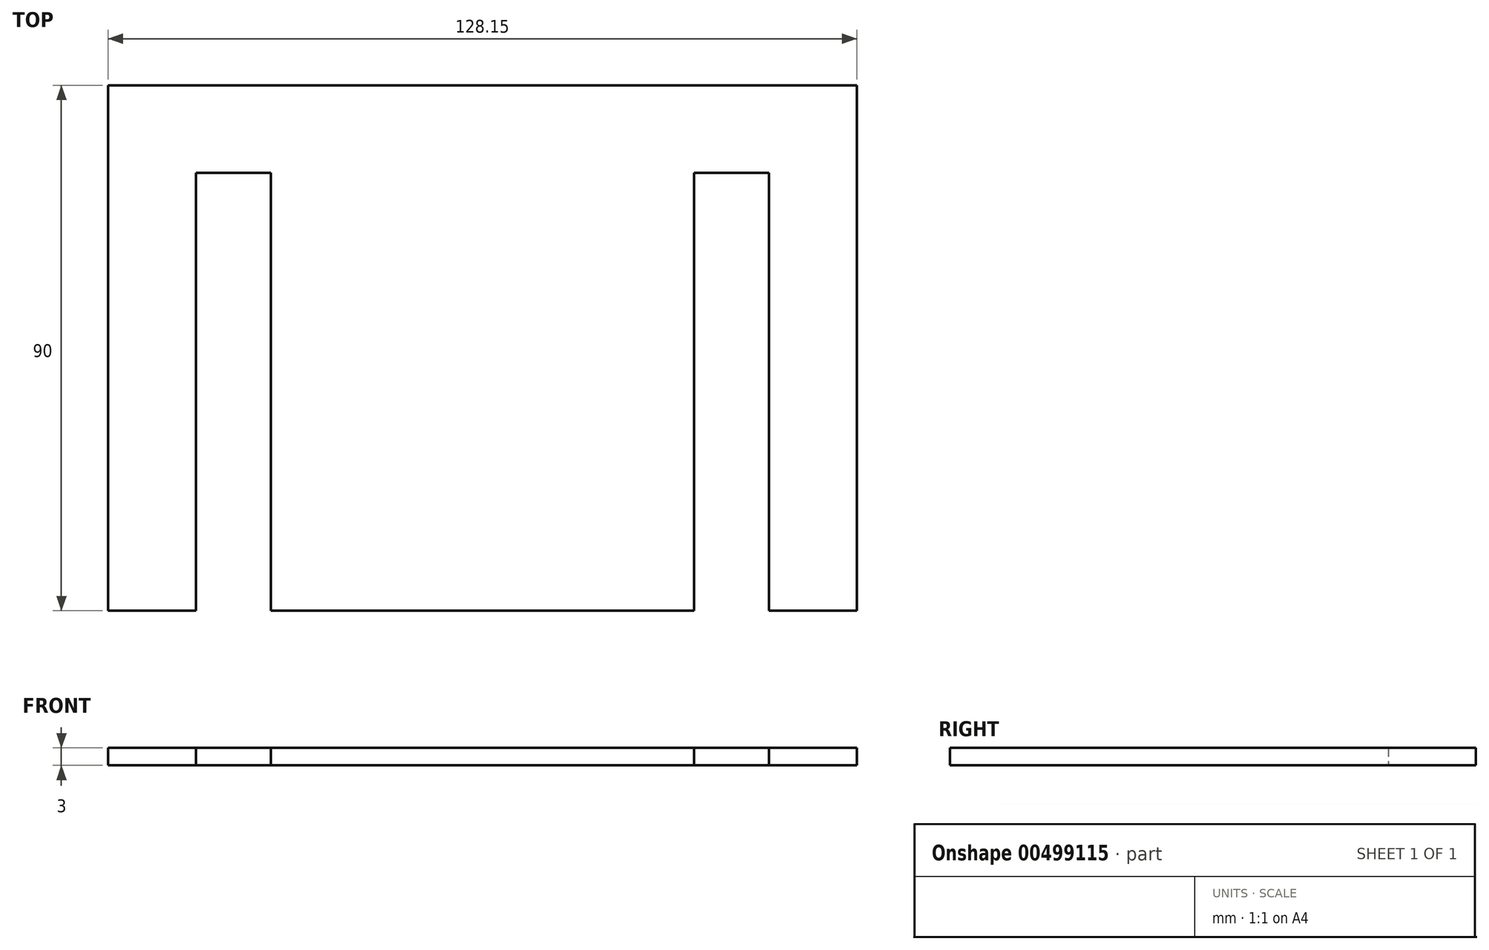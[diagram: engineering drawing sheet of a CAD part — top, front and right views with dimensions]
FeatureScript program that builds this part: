
annotation { "Feature Type Name" : "Feature", "Feature Type Description" : "" }
export const myFeature = defineFeature(function(context is Context, id is Id, definition is map)
    precondition{}
    {
        {
            var Q0;
            Q0=qCreatedBy(makeId("Top.planeOp"),FACE);
            var sketch = newSketch(context, id + "F0", { "sketchPlane" : qUnion([Q0])});
            skLineSegment(sketch, "E0.bottom", {"start": v(-48.74, 60.3) * mm, "end": v(49.4, 60.3) * mm});
            skPoint(sketch, "E0.middle", {"position": v(0.33, 15.34) * mm});
            skLineSegment(sketch, "E1", {"start": v(-35.92, -29.7) * mm, "end": v(-35.92, 45.3) * mm});
            skLineSegment(sketch, "E2", {"start": v(36.58, -29.7) * mm, "end": v(36.58, 45.3) * mm});
            skLineSegment(sketch, "E3", {"start": v(-35.92, -29.7) * mm, "end": v(36.58, -29.7) * mm});
            skLineSegment(sketch, "E4.bottom", {"start": v(-48.74, 60.3) * mm, "end": v(-63.74, 60.3) * mm});
            skLineSegment(sketch, "E4.top", {"start": v(-48.74, -29.7) * mm, "end": v(-63.74, -29.7) * mm});
            skLineSegment(sketch, "E4.right", {"start": v(-63.74, 60.3) * mm, "end": v(-63.74, -29.7) * mm});
            skLineSegment(sketch, "E5.bottom", {"start": v(49.4, 60.3) * mm, "end": v(64.4, 60.3) * mm});
            skLineSegment(sketch, "E5.top", {"start": v(49.4, -29.7) * mm, "end": v(64.4, -29.7) * mm});
            skLineSegment(sketch, "E5.right", {"start": v(64.4, 60.3) * mm, "end": v(64.4, -29.7) * mm});
            skLineSegment(sketch, "E6", {"start": v(-35.92, 45.3) * mm, "end": v(-48.74, 45.3) * mm});
            skLineSegment(sketch, "E7", {"start": v(36.58, 45.3) * mm, "end": v(49.4, 45.3) * mm});
            skLineSegment(sketch, "E8", {"start": v(-48.74, 45.3) * mm, "end": v(-48.74, -29.7) * mm});
            skLineSegment(sketch, "E9", {"start": v(49.4, 45.3) * mm, "end": v(49.4, -29.7) * mm});
            skSolve(sketch);
        }
        {
            var Q0;
            Q0=makeQuery(id+"F0.imprint","IMPRINT",FACE,{"disambiguationData":[TD([[makeQuery(id+"F0.imprint","IMPRINT",EDGE,{"derivedFrom":sQuery(id+"F0.wireOp",EDGE,"E0.bottom")}),-1.0]])]});
            extrude(context, id + "F1", {"entities" : qUnion([Q0]), "depth" : 3 * mm});
        }
    });
